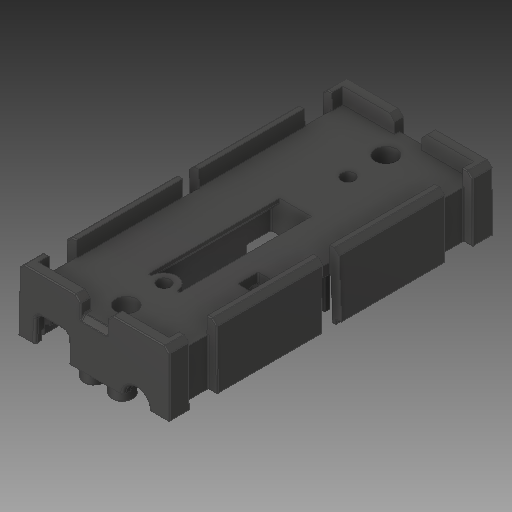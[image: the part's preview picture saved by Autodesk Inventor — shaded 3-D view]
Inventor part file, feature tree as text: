
AUTODESK INVENTOR PART (.ipt)
format: ipt  version: 2019 (Build 230136000, 136)  size: 2,923,520 bytes
history: native  units: in
note: dims shown in document units (in); Inventor stores cm internally (conversion verified against a paired STEP export)
features: fillet x1
ambient origin geometry x8: Origin, YZ Plane, XZ Plane, XY Plane, X Axis, Y Axis, Z Axis, Center Point
bodies: Solid1 (feature_tree)
feature tree (1):
  fillet  "Fillet20"  [1 undecoded]
note: 1 required parameter value undecoded (feature->parameter linkage not recoverable at this tier; creation-order binding heuristic only, values carry confidence <= 0.55)
